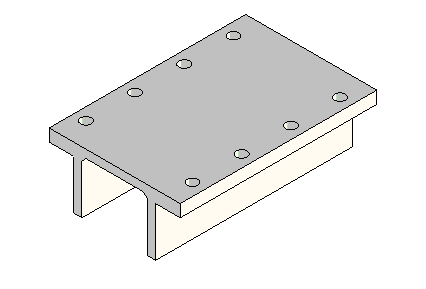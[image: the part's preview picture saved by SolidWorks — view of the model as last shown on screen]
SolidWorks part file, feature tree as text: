
SOLIDWORKS PART (.sldprt)
format: sldprt  version: not decoded by parser v0  size: 222,208 bytes
history: native  units: mm
features: sketch x5, extrude x2, hole x1, cut_extrude x1 (+11 scaffold rows collapsed)
feature tree (20):
  scaffold x11  (default folders/planes/origin — collapsed)
  sketch  "Sketch1"  dims[D1=152.4mm D2=101.6mm]
  extrude  "Extrude1"  Depth=9.525mm
  hole  "21/64 (0.328130) Diameter Hole1"  Diameter=8.334502mm Depth=9.525mm
  sketch  "Sketch3"  dims[D1=9.525mm D2=9.525mm D3=19.05mm D4=19.05mm D5=38.1mm D6=38.1mm D7=38.1mm D8=19.05mm D9=38.1mm D10=38.1mm D11=38.1mm D12=19.05mm D13=82.55mm]
  sketch  "Sketch2"  dims[hole-wizard template sketch: 59 standard entries collapsed; hole parameters kept: c18.Thru Hole Dia.=~8.334502mm c18.Thru Hole Depth=9.525mm]
  sketch  "Sketch4"  dims[D1=63.5mm]
  extrude  "Extrude2"  Depth=38.1mm
  sketch  "Sketch5"  dims[c1.D1=~36.898558mm c2.D1=45.0deg c2.D2=~36.898558mm c3.D2=45.0deg c3.D3=6.35mm c3.D4=6.35mm c3.D5=6.35mm]
  cut_extrude  "Cut-Extrude1"  [1 undecoded]
decode coverage: 8 of 9 modeling features carry decoded parameters
note: ~ marks probable driven/reference dimensions
note: 1 parameter value undecoded
note: suppression state not decoded; provenance and decode notes live in map.json
